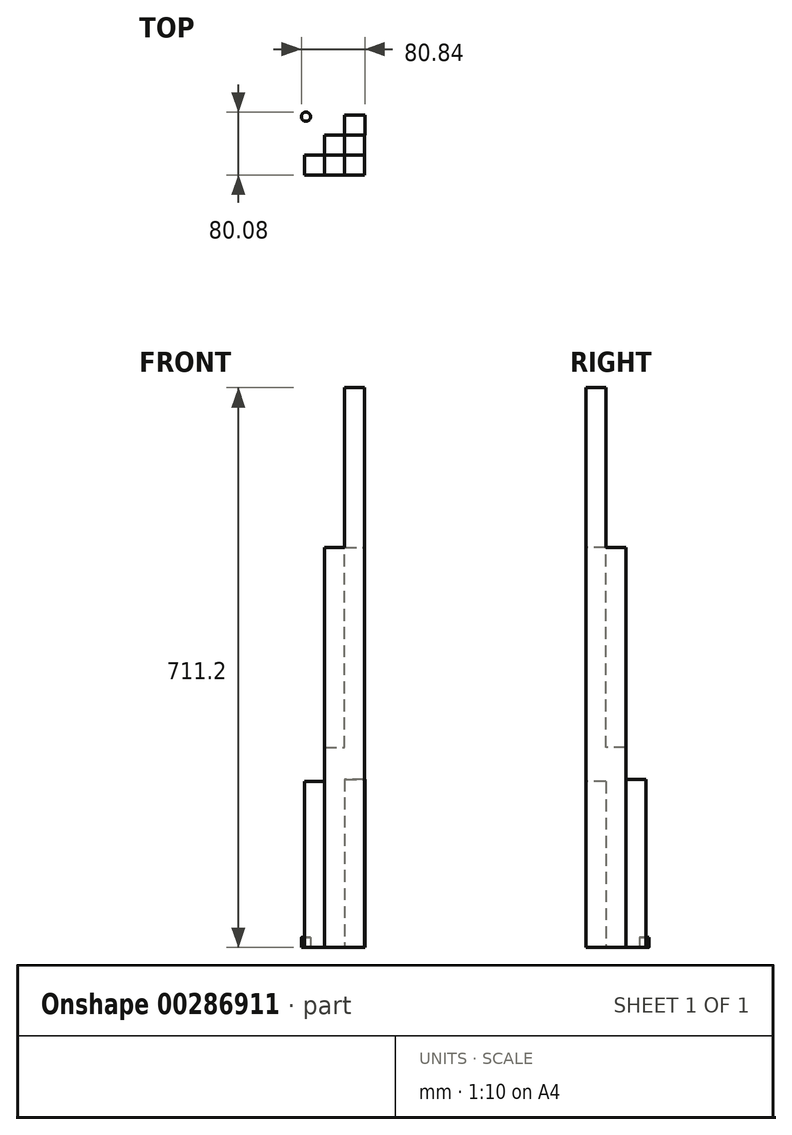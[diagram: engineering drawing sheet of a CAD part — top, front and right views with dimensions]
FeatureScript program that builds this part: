
annotation { "Feature Type Name" : "Feature", "Feature Type Description" : "" }
export const myFeature = defineFeature(function(context is Context, id is Id, definition is map)
    precondition{}
    {
        {
            var Q0;
            Q0=qCreatedBy(makeId("Top.planeOp"),FACE);
            var sketch = newSketch(context, id + "F0", { "sketchPlane" : qUnion([Q0])});
            skLineSegment(sketch, "E0.bottom", {"start": v(0, 0) * mm, "end": v(50.8, 0) * mm});
            skLineSegment(sketch, "E0.top", {"start": v(0, -50.8) * mm, "end": v(50.8, -50.8) * mm});
            skLineSegment(sketch, "E0.left", {"start": v(0, 0) * mm, "end": v(0, -50.8) * mm});
            skLineSegment(sketch, "E0.right", {"start": v(50.8, 0) * mm, "end": v(50.8, -50.8) * mm});
            skSolve(sketch);
        }
        {
            var Q0;
            Q0 = qSketchRegion(id + "F0", true);
            extrude(context, id + "F1", {"entities" : qUnion([Q0]), "depth" : 508 * mm});
        }
        {
            var Q0;
            Q0=makeQuery(id+"F1.opExtrude","CAP_FACE",FACE,{"disambiguationData":[OSD([sQuery(id+"F0.wireOp",EDGE,"E0.bottom"),sQuery(id+"F0.wireOp",EDGE,"E0.top"),sQuery(id+"F0.wireOp",EDGE,"E0.left"),sQuery(id+"F0.wireOp",EDGE,"E0.right")])],"isStart":false});
            var sketch = newSketch(context, id + "F2", { "sketchPlane" : qUnion([Q0])});
            skLineSegment(sketch, "E1", {"start": v(25.4, 0) * mm, "end": v(25.4, -25.4) * mm});
            skPoint(sketch, "E1.endSnap0", {"position": v(0, -25.4) * mm});
            skLineSegment(sketch, "E2", {"start": v(25.4, -25.4) * mm, "end": v(0, -25.4) * mm});
            skLineSegment(sketch, "E3", {"start": v(0, -25.4) * mm, "end": v(0, 0) * mm});
            skLineSegment(sketch, "E4", {"start": v(0, 0) * mm, "end": v(25.4, 0) * mm});
            skSolve(sketch);
        }
        {
            var Q0;
            Q0 = qSketchRegion(id + "F2", true);
            extrude(context, id + "F3", {"entities" : qUnion([Q0]), "operationType" : NewBodyOperationType.REMOVE, "oppositeDirection" : true, "depth" : 254 * mm});
        }
        {
            var Q0;
            Q0=makeQuery(id+"F1.opExtrude","CAP_FACE",FACE,{"disambiguationData":[OSD([sQuery(id+"F0.wireOp",EDGE,"E0.bottom"),sQuery(id+"F0.wireOp",EDGE,"E0.top"),sQuery(id+"F0.wireOp",EDGE,"E0.left"),sQuery(id+"F0.wireOp",EDGE,"E0.right")])],"isStart":false});
            var sketch = newSketch(context, id + "F4", { "sketchPlane" : qUnion([Q0])});
            skLineSegment(sketch, "E5", {"start": v(25.4, -25.4) * mm, "end": v(25.4, -50.8) * mm});
            skLineSegment(sketch, "E6", {"start": v(25.4, -50.8) * mm, "end": v(50.8, -50.8) * mm});
            skLineSegment(sketch, "E7", {"start": v(50.8, -50.8) * mm, "end": v(50.8, -25.4) * mm});
            skLineSegment(sketch, "E8", {"start": v(50.8, -25.4) * mm, "end": v(25.4, -25.4) * mm});
            skSolve(sketch);
        }
        {
            var Q0;
            Q0 = qSketchRegion(id + "F4", true);
            extrude(context, id + "F5", {"entities" : qUnion([Q0]), "operationType" : NewBodyOperationType.ADD, "depth" : 203.2 * mm});
        }
        {
            var Q0;
            Q0=qCreatedBy(makeId("Top.planeOp"),FACE);
            var sketch = newSketch(context, id + "F6", { "sketchPlane" : qUnion([Q0])});
            skLineSegment(sketch, "E9", {"start": v(25.6, 0) * mm, "end": v(25.6, 25.4) * mm});
            skLineSegment(sketch, "E10", {"start": v(25.6, 25.4) * mm, "end": v(51.39, 25.4) * mm});
            skLineSegment(sketch, "E11", {"start": v(51.39, 25.4) * mm, "end": v(51.39, 0) * mm});
            skLineSegment(sketch, "E12", {"start": v(51.39, 0) * mm, "end": v(25.6, 0) * mm});
            skLineSegment(sketch, "E13", {"start": v(0, -25.1) * mm, "end": v(-25.4, -25.1) * mm});
            skLineSegment(sketch, "E14", {"start": v(0, -50.22) * mm, "end": v(-25.4, -50.22) * mm});
            skLineSegment(sketch, "E15", {"start": v(-25.4, -50.22) * mm, "end": v(-25.4, -25.1) * mm});
            skSolve(sketch);
        }
        {
            var Q0;
            Q0 = qSketchRegion(id + "F6", true);
            extrude(context, id + "F7", {"entities" : qUnion([Q0]), "operationType" : NewBodyOperationType.ADD, "depth" : 213.36 * mm});
        }
        {
            var Q0;
            Q0=qCreatedBy(makeId("Top.planeOp"),FACE);
            var sketch = newSketch(context, id + "F8", { "sketchPlane" : qUnion([Q0])});
            skLineSegment(sketch, "E16", {"start": v(0, -25.44) * mm, "end": v(-25.4, -25.44) * mm});
            skLineSegment(sketch, "E17", {"start": v(0, -50.55) * mm, "end": v(-25.4, -50.55) * mm});
            skLineSegment(sketch, "E18", {"start": v(-25.4, -50.55) * mm, "end": v(-25.4, -25.44) * mm});
            skLineSegment(sketch, "E19", {"start": v(0, -25.44) * mm, "end": v(0, -50.55) * mm});
            skSolve(sketch);
        }
        {
            var Q0;
            Q0 = qSketchRegion(id + "F8", true);
            extrude(context, id + "F9", {"entities" : qUnion([Q0]), "operationType" : NewBodyOperationType.ADD, "depth" : 210.82 * mm});
        }
        {
            var Q0;
            Q0=qCreatedBy(makeId("Top.planeOp"),FACE);
            var sketch = newSketch(context, id + "F10", { "sketchPlane" : qUnion([Q0])});
            skLineSegment(sketch, "E20", {"start": v(0, 0) * mm, "end": v(-23.6, 23.43) * mm});
            skCircle(sketch, "E21", {"center": v(-23.6, 23.43) * mm, "radius": 5.85 * mm});
            skSolve(sketch);
        }
        {
            var Q0;
            Q0 = qSketchRegion(id + "F10", true);
            extrude(context, id + "F11", {"entities" : qUnion([Q0]), "depth" : 12.7 * mm});
        }
    });
